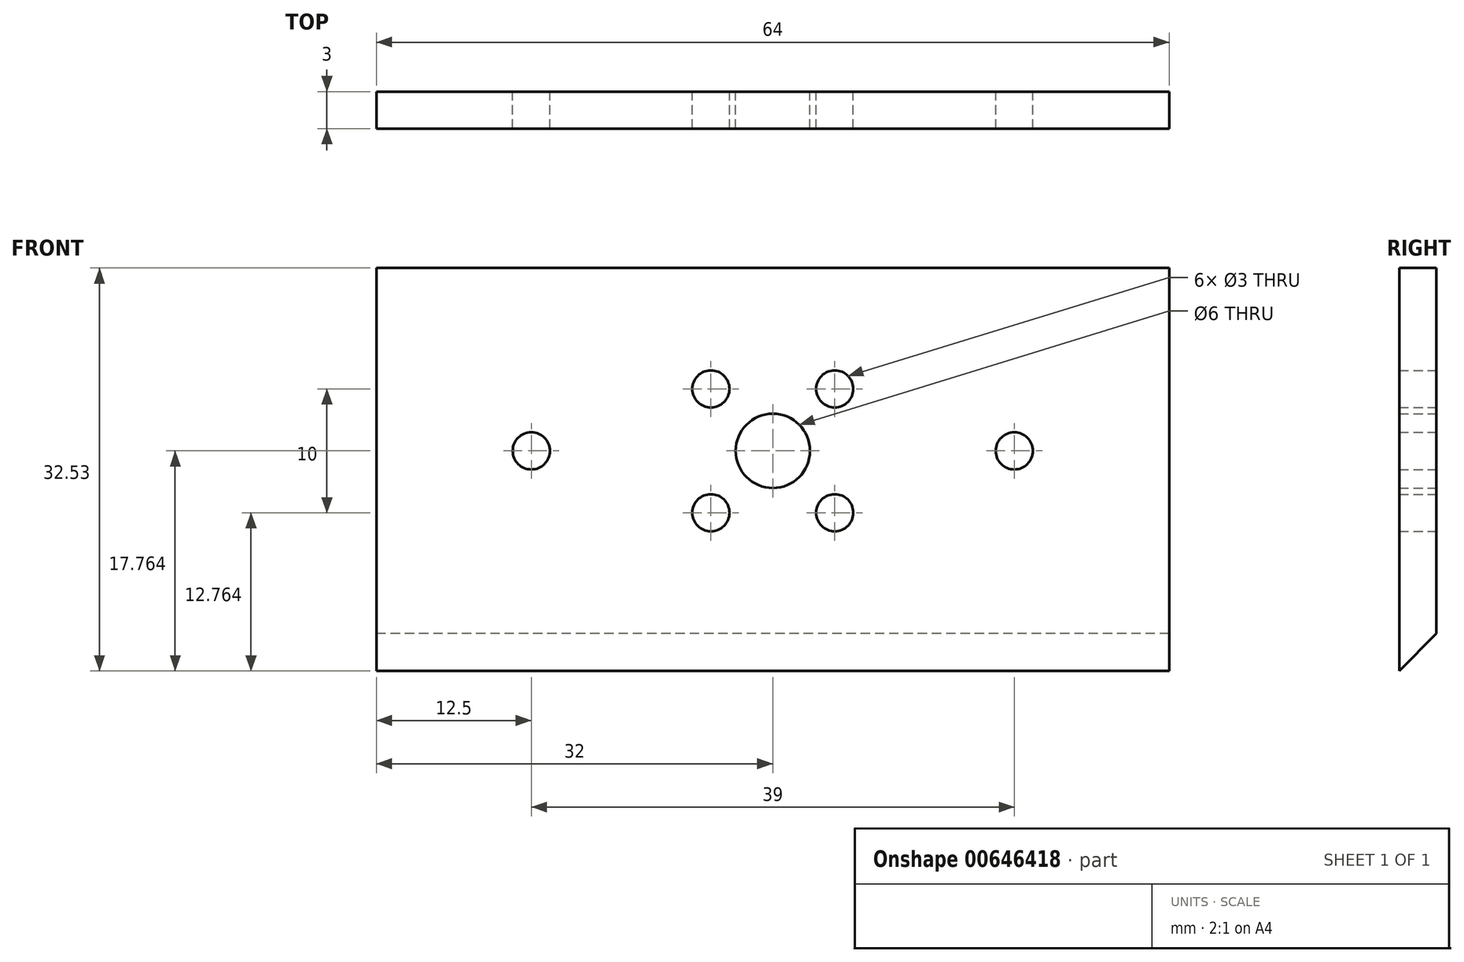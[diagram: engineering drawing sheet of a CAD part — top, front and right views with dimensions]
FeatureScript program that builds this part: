
annotation { "Feature Type Name" : "Feature", "Feature Type Description" : "" }
export const myFeature = defineFeature(function(context is Context, id is Id, definition is map)
    precondition{}
    {
        {
            var Q0;
            Q0=qCreatedBy(makeId("Front.planeOp"),FACE);
            var sketch = newSketch(context, id + "F0", { "sketchPlane" : qUnion([Q0])});
            skLineSegment(sketch, "E0.bottom", {"start": v(0, 0) * mm, "end": v(-64, 0) * mm});
            skLineSegment(sketch, "E0.top", {"start": v(0, 32.53) * mm, "end": v(-64, 32.53) * mm});
            skLineSegment(sketch, "E0.left", {"start": v(0, 0) * mm, "end": v(0, 32.53) * mm});
            skLineSegment(sketch, "E0.right", {"start": v(-64, 0) * mm, "end": v(-64, 32.53) * mm});
            skSolve(sketch);
        }
        {
            var Q0;
            Q0=makeQuery(id+"F0.imprint","IMPRINT",FACE,{"disambiguationData":[TD([[makeQuery(id+"F0.imprint","IMPRINT",EDGE,{"derivedFrom":sQuery(id+"F0.wireOp",EDGE,"E0.bottom")}),-1.0]])]});
            extrude(context, id + "F1", {"entities" : qUnion([Q0]), "depth" : 3 * mm, "offsetDistance" : 25 * mm});
        }
        {
            var Q0;
            Q0=makeQuery(id+"F1.opExtrude","CAP_EDGE",EDGE,{"disambiguationData":[OSD([sQuery(id+"F0.wireOp",EDGE,"E0.bottom")])],"isStart":true});
            chamfer(context, id + "F2", {"entities" : qUnion([Q0]), "width" : 3 * mm, "tangentPropagation" : true});
        }
        {
            var Q0;
            Q0=makeQuery(id+"F1.opExtrude","SWEPT_FACE",FACE,{"disambiguationData":[OSD([sQuery(id+"F0.wireOp",EDGE,"E0.right")])]});
            var sketch = newSketch(context, id + "F3", { "sketchPlane" : qUnion([Q0])});
            skLineSegment(sketch, "E1", {"start": v(3, 0) * mm, "end": v(-23.6, 26.6) * mm});
            skLineSegment(sketch, "E2", {"start": v(3, 32.53) * mm, "end": v(-23.6, 59.14) * mm});
            skLineSegment(sketch, "E3", {"start": v(-23.6, 59.14) * mm, "end": v(-23.6, 26.6) * mm});
            skSolve(sketch);
        }
        {
            var Q0;
            Q0=makeQuery(id+"F1.opExtrude","SWEPT_FACE",FACE,{"disambiguationData":[OSD([sQuery(id+"F0.wireOp",EDGE,"E0.left")])]});
            var sketch = newSketch(context, id + "F4", { "sketchPlane" : qUnion([Q0])});
            skLineSegment(sketch, "E4", {"start": v(-3, 32.53) * mm, "end": v(23.6, 59.14) * mm});
            skLineSegment(sketch, "E5", {"start": v(23.6, 59.14) * mm, "end": v(23.6, 26.6) * mm});
            skLineSegment(sketch, "E6", {"start": v(23.6, 26.6) * mm, "end": v(-3, 0) * mm});
            skSolve(sketch);
        }
        {
            var Q0;
            Q0=makeQuery(id+"F1.opExtrude","CAP_FACE",FACE,{"disambiguationData":[OSD([sQuery(id+"F0.wireOp",EDGE,"E0.bottom"),sQuery(id+"F0.wireOp",EDGE,"E0.top"),sQuery(id+"F0.wireOp",EDGE,"E0.left"),sQuery(id+"F0.wireOp",EDGE,"E0.right")])],"isStart":true});
            var sketch = newSketch(context, id + "F5", { "sketchPlane" : qUnion([Q0])});
            skLineSegment(sketch, "E7", {"start": v(32, 32.53) * mm, "end": v(32, 3) * mm, "construction": true});
            skLineSegment(sketch, "E8", {"start": v(0, 17.76) * mm, "end": v(32, 17.76) * mm, "construction": true});
            skLineSegment(sketch, "E9", {"start": v(32, 17.76) * mm, "end": v(32, 22.76) * mm, "construction": true});
            skLineSegment(sketch, "E10", {"start": v(32, 22.76) * mm, "end": v(37, 22.76) * mm, "construction": true});
            skLineSegment(sketch, "E11.bottom", {"start": v(37, 22.76) * mm, "end": v(27, 22.76) * mm, "construction": true});
            skLineSegment(sketch, "E11.top", {"start": v(37, 12.76) * mm, "end": v(27, 12.76) * mm, "construction": true});
            skLineSegment(sketch, "E11.left", {"start": v(37, 22.76) * mm, "end": v(37, 12.76) * mm, "construction": true});
            skLineSegment(sketch, "E11.right", {"start": v(27, 22.76) * mm, "end": v(27, 12.76) * mm, "construction": true});
            skLineSegment(sketch, "E12", {"start": v(32, 17.76) * mm, "end": v(51.5, 17.76) * mm, "construction": true});
            skLineSegment(sketch, "E13", {"start": v(32, 17.76) * mm, "end": v(12.5, 17.76) * mm, "construction": true});
            skSolve(sketch);
        }
        {
            var Q0;
            Q0=sQuery(id+"F5.wireOp",VERTEX,"E8.end");
            var Q1;
            Q1=makeQuery(id+"F1.opExtrude","SWEPT_BODY",BODY,{"disambiguationData":[OSD([sQuery(id+"F0.wireOp",EDGE,"E0.bottom"),sQuery(id+"F0.wireOp",EDGE,"E0.top"),sQuery(id+"F0.wireOp",EDGE,"E0.left"),sQuery(id+"F0.wireOp",EDGE,"E0.right")])]});
            hole(context, id + "F6", {"style" : HoleStyle.SIMPLE, "endStyle" : HoleEndStyle.THROUGH, "holeDiameter" : 6 * mm, "majorDiameter" : 5 * mm, "isTappedThrough" : true, "tappedDepth" : 12 * mm, "tapClearance" : 3, "locations" : qUnion([Q0]), "scope" : qUnion([Q1])});
        }
        {
            var Q0;
            Q0=sQuery(id+"F5.wireOp",VERTEX,"E10.end");
            var Q1;
            Q1=sQuery(id+"F5.wireOp",VERTEX,"E11.right.start");
            var Q2;
            Q2=sQuery(id+"F5.wireOp",VERTEX,"E11.right.end");
            var Q3;
            Q3=sQuery(id+"F5.wireOp",VERTEX,"E11.left.end");
            var Q4;
            Q4=sQuery(id+"F5.wireOp",VERTEX,"E13.end");
            var Q5;
            Q5=sQuery(id+"F5.wireOp",VERTEX,"E12.end");
            var Q6;
            Q6=makeQuery(id+"F1.opExtrude","SWEPT_BODY",BODY,{"disambiguationData":[OSD([sQuery(id+"F0.wireOp",EDGE,"E0.bottom"),sQuery(id+"F0.wireOp",EDGE,"E0.top"),sQuery(id+"F0.wireOp",EDGE,"E0.left"),sQuery(id+"F0.wireOp",EDGE,"E0.right")])]});
            hole(context, id + "F7", {"style" : HoleStyle.SIMPLE, "endStyle" : HoleEndStyle.THROUGH, "holeDiameter" : 3 * mm, "majorDiameter" : 5 * mm, "isTappedThrough" : true, "tappedDepth" : 12 * mm, "tapClearance" : 3, "locations" : qUnion([Q0, Q1, Q2, Q3, Q4, Q5]), "scope" : qUnion([Q6])});
        }
    });
